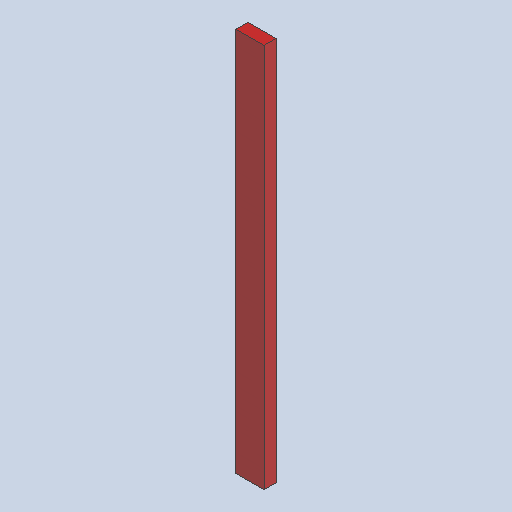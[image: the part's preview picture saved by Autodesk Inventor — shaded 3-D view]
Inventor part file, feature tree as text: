
AUTODESK INVENTOR PART (.ipt)
format: ipt  version: 2025 (Build 290162000, 162)  size: 88,576 bytes
history: native  units: in
note: dims shown in document units (in); Inventor stores cm internally (conversion verified against a paired STEP export)
features: other x4, sketch x1
ambient origin geometry x8: Origin, YZ Plane, XZ Plane, XY Plane, X Axis, Y Axis, Z Axis, Center Point
bodies: Solid1 (feature_tree)
feature tree (5):
  other  "8'x2x4.ipt"
  other  "Solid1::8'x2x4.ipt"
  other  "TaggingFeature1"
  sketch  "Sketch1"  dims[d0=0.3937in]
  other  "Finish1"
